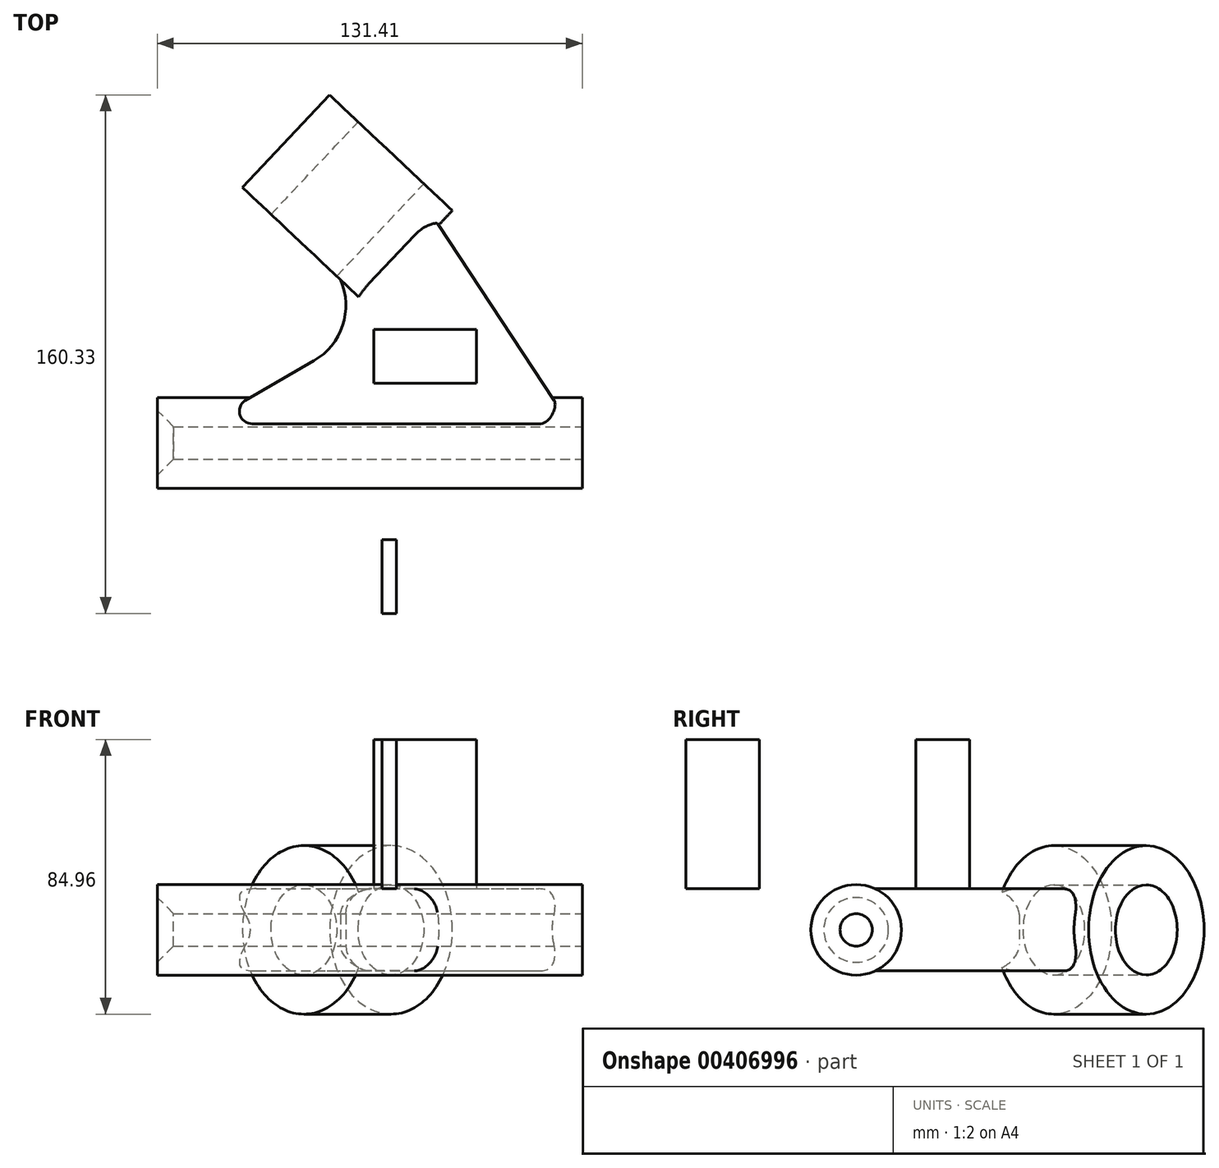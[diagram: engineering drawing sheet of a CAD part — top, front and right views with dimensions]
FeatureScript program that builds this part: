
annotation { "Feature Type Name" : "Feature", "Feature Type Description" : "" }
export const myFeature = defineFeature(function(context is Context, id is Id, definition is map)
    precondition{}
    {
        {
            var Q0;
            Q0=qCreatedBy(makeId("Top.planeOp"),FACE);
            var sketch = newSketch(context, id + "F0", { "sketchPlane" : qUnion([Q0])});
            skLineSegment(sketch, "E0", {"start": v(0, 0) * mm, "end": v(-127, 0) * mm});
            skLineSegment(sketch, "E1", {"start": v(-127, 0) * mm, "end": v(-83, 25.4) * mm});
            skArc(sketch, "E2", {"start": v(-83, 25.4) * mm, "mid": v(-73.18, 44.25) * mm, "end": v(-86.1, 61.13) * mm});
            skLineSegment(sketch, "E3", {"start": v(-86.1, 61.13) * mm, "end": v(-59.16, 89.74) * mm});
            skLineSegment(sketch, "E4", {"start": v(-59.16, 89.74) * mm, "end": v(0, 0) * mm});
            skLineSegment(sketch, "E5", {"start": v(-59.16, 89.74) * mm, "end": v(-78.13, 107.6) * mm});
            skLineSegment(sketch, "E6", {"start": v(-78.13, 107.6) * mm, "end": v(-105.07, 79) * mm});
            skLineSegment(sketch, "E7", {"start": v(-105.07, 79) * mm, "end": v(-86.1, 61.13) * mm});
            skSolve(sketch);
        }
        {
            var Q0;
            Q0=makeQuery(id+"F0.imprint","IMPRINT",FACE,{"disambiguationData":[TD([[makeQuery(id+"F0.imprint","IMPRINT",EDGE,{"derivedFrom":sQuery(id+"F0.wireOp",EDGE,"E0")}),-1.0]])]});
            extrude(context, id + "F1", {"entities" : qUnion([Q0]), "endBound" : BoundingType.SYMMETRIC, "depth" : 25.4 * mm});
        }
        {
            var Q0;
            Q0=makeQuery(id+"F0.imprint","IMPRINT",FACE,{"disambiguationData":[TD([[makeQuery(id+"F0.imprint","IMPRINT",EDGE,{"derivedFrom":sQuery(id+"F0.wireOp",EDGE,"E3")}),1.0]])]});
            var Q1;
            Q1=sQuery(id+"F0.wireOp",EDGE,"E3");
            revolve(context, id + "F2", {"operationType" : NewBodyOperationType.ADD, "entities" : qUnion([Q0]), "axis" : qUnion([Q1]), "revolveType" : RevolveType.FULL});
        }
        {
            var Q0;
            Q0=makeQuery(id+"F2.opRevolve","SWEPT_FACE",FACE,{"disambiguationData":[OSD([sQuery(id+"F0.wireOp",EDGE,"E5")])]});
            var sketch = newSketch(context, id + "F3", { "sketchPlane" : qUnion([Q0])});
            skCircle(sketch, "E8", {"center": v(104.59, 0) * mm, "radius": 13.95 * mm});
            skSolve(sketch);
        }
        {
            var Q0;
            Q0=makeQuery(id+"F3.imprint","IMPRINT",FACE,{"disambiguationData":[TD([[makeQuery(id+"F3.imprint","IMPRINT",EDGE,{"derivedFrom":sQuery(id+"F3.wireOp",EDGE,"E8")}),1.0]])]});
            extrude(context, id + "F4", {"entities" : qUnion([Q0]), "operationType" : NewBodyOperationType.REMOVE, "endBound" : BoundingType.UP_TO_NEXT, "oppositeDirection" : true, "depth" : 25.4 * mm});
        }
        {
            var Q0;
            Q0=qCreatedBy(makeId("Right.planeOp"),FACE);
            var sketch = newSketch(context, id + "F5", { "sketchPlane" : qUnion([Q0])});
            skCircle(sketch, "E9", {"center": v(0, 0) * mm, "radius": 14 * mm});
            skSolve(sketch);
        }
        {
            var Q0;
            Q0=makeQuery(id+"F5.imprint","IMPRINT",FACE,{"disambiguationData":[TD([[makeQuery(id+"F5.imprint","IMPRINT",EDGE,{"derivedFrom":sQuery(id+"F5.wireOp",EDGE,"E9")}),1.0]])]});
            var Q1;
            Q1=sQuery(id+"F5.wireOp",EDGE,"E9");
            extrude(context, id + "F6", {"entities" : qUnion([Q0]), "operationType" : NewBodyOperationType.ADD, "surfaceEntities" : qUnion([Q1]), "oppositeDirection" : true, "depth" : 131.4 * mm});
        }
        {
            var Q0;
            Q0=makeQuery(id+"F5.imprint","IMPRINT",FACE,{"disambiguationData":[TD([[makeQuery(id+"F5.imprint","IMPRINT",EDGE,{"derivedFrom":sQuery(id+"F5.wireOp",EDGE,"E9")}),1.0]])]});
            var sketch = newSketch(context, id + "F7", { "sketchPlane" : qUnion([Q0])});
            skCircle(sketch, "E10", {"center": v(0, 0) * mm, "radius": 5 * mm});
            skSolve(sketch);
        }
        {
            var Q0;
            Q0 = qSketchRegion(id + "F7", true);
            extrude(context, id + "F8", {"entities" : qUnion([Q0]), "operationType" : NewBodyOperationType.REMOVE, "endBound" : BoundingType.THROUGH_ALL, "oppositeDirection" : true, "depth" : 25 * mm});
        }
        {
            var Q0;
            Q0=makeQuery(id+"F8.boolean.opBoolean","COPY",EDGE,{"derivedFrom":makeQuery(id+"F8.opExtrude","CAP_EDGE",EDGE,{"disambiguationData":[OSD([sQuery(id+"F7.wireOp",EDGE,"E10")])],"isStart":true})});
            var Q1;
            Q1=makeQuery(id+"F8.boolean.opBoolean","INTERSECT",EDGE,{"derivedFrom":[makeQuery(id+"F6.opExtrude","CAP_FACE",FACE,{"disambiguationData":[OSD([sQuery(id+"F5.wireOp",EDGE,"E9")])],"isStart":false}),makeQuery(id+"F8.opExtrude","SWEPT_FACE",FACE,{"disambiguationData":[OSD([sQuery(id+"F7.wireOp",EDGE,"E10")])]})]});
            chamfer(context, id + "F9", {"entities" : qUnion([Q0, Q1]), "width" : 5 * mm, "tangentPropagation" : true});
        }
        {
            var Q0;
            Q0=makeQuery(id+"F1.opExtrude","CAP_EDGE",EDGE,{"disambiguationData":[OSD([sQuery(id+"F0.wireOp",EDGE,"E4")])],"isStart":false});
            var Q1;
            Q1=makeQuery(id+"F1.opExtrude","CAP_EDGE",EDGE,{"disambiguationData":[OSD([sQuery(id+"F0.wireOp",EDGE,"E2")])],"isStart":true});
            var Q2;
            Q2=makeQuery(id+"F1.opExtrude","CAP_EDGE",EDGE,{"disambiguationData":[OSD([sQuery(id+"F0.wireOp",EDGE,"E4")])],"isStart":true});
            var Q3;
            Q3=makeQuery(id+"F1.opExtrude","CAP_EDGE",EDGE,{"disambiguationData":[OSD([sQuery(id+"F0.wireOp",EDGE,"E2")])],"isStart":false});
            var Q4;
            Q4=makeQuery(id+"F1.opExtrude","CAP_EDGE",EDGE,{"disambiguationData":[OSD([sQuery(id+"F0.wireOp",EDGE,"E1")])],"isStart":false});
            var Q5;
            Q5=makeQuery(id+"F1.opExtrude","CAP_EDGE",EDGE,{"disambiguationData":[OSD([sQuery(id+"F0.wireOp",EDGE,"E1")])],"isStart":true});
            fillet(context, id + "F10", {"entities" : qUnion([Q0, Q1, Q2, Q3, Q4, Q5]), "radius" : 8 * mm, "tangentPropagation" : true, "allowEdgeOverflow" : false});
        }
        {
            var Q0;
            Q0=makeQuery(id+"F1.opExtrude","CAP_FACE",FACE,{"disambiguationData":[OSD([sQuery(id+"F0.wireOp",EDGE,"E0"),sQuery(id+"F0.wireOp",EDGE,"E1"),sQuery(id+"F0.wireOp",EDGE,"E2"),sQuery(id+"F0.wireOp",EDGE,"E3"),sQuery(id+"F0.wireOp",EDGE,"E4")])],"isStart":false});
            var sketch = newSketch(context, id + "F11", { "sketchPlane" : qUnion([Q0])});
            skLineSegment(sketch, "E11.bottom", {"start": v(-64.5, 18.4) * mm, "end": v(-32.7, 18.4) * mm});
            skLineSegment(sketch, "E11.top", {"start": v(-64.5, 35.06) * mm, "end": v(-32.7, 35.06) * mm});
            skLineSegment(sketch, "E11.left", {"start": v(-64.5, 18.4) * mm, "end": v(-64.5, 35.06) * mm});
            skLineSegment(sketch, "E11.right", {"start": v(-32.7, 18.4) * mm, "end": v(-32.7, 35.06) * mm});
            skLineSegment(sketch, "E12.bottom", {"start": v(-61.95, -29.98) * mm, "end": v(-57.47, -29.98) * mm});
            skLineSegment(sketch, "E12.top", {"start": v(-61.95, -52.72) * mm, "end": v(-57.47, -52.72) * mm});
            skLineSegment(sketch, "E12.left", {"start": v(-61.95, -29.98) * mm, "end": v(-61.95, -52.72) * mm});
            skLineSegment(sketch, "E12.right", {"start": v(-57.47, -29.98) * mm, "end": v(-57.47, -52.72) * mm});
            skSolve(sketch);
        }
        {
            var Q0;
            Q0 = qSketchRegion(id + "F11", true);
            extrude(context, id + "F12", {"entities" : qUnion([Q0]), "operationType" : NewBodyOperationType.ADD, "depth" : 46.2 * mm, "offsetDistance" : 25 * mm});
        }
    });
